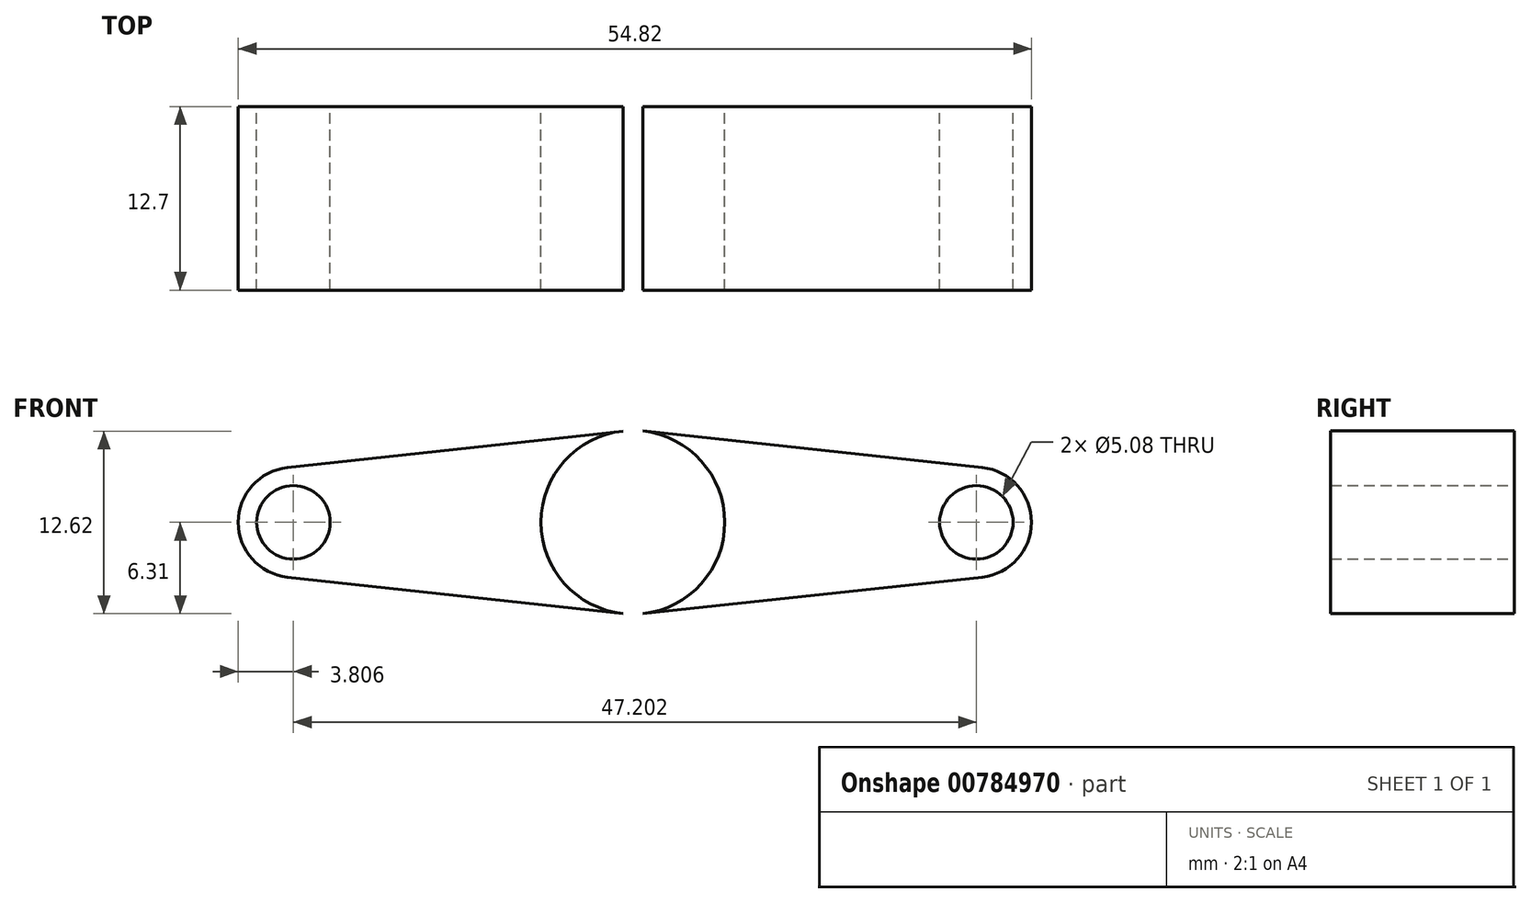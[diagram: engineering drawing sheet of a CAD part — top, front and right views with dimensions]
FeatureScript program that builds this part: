
annotation { "Feature Type Name" : "Feature", "Feature Type Description" : "" }
export const myFeature = defineFeature(function(context is Context, id is Id, definition is map)
    precondition{}
    {
        {
            var Q0;
            Q0=qCreatedBy(makeId("Front.planeOp"),FACE);
            var sketch = newSketch(context, id + "F0", { "sketchPlane" : qUnion([Q0])});
            skLineSegment(sketch, "E0", {"start": v(-23.46, 0) * mm, "end": v(23.74, 0) * mm});
            skCircle(sketch, "E1", {"center": v(23.74, 0) * mm, "radius": 3.81 * mm});
            skCircle(sketch, "E2", {"center": v(0, 0) * mm, "radius": 6.35 * mm});
            skCircle(sketch, "E3", {"center": v(-23.46, 0) * mm, "radius": 3.81 * mm});
            skLineSegment(sketch, "E4", {"start": v(-23.88, -3.79) * mm, "end": v(-0.69, -6.31) * mm});
            skLineSegment(sketch, "E5", {"start": v(-23.88, 3.79) * mm, "end": v(-0.69, 6.31) * mm});
            skLineSegment(sketch, "E6", {"start": v(0.68, 6.31) * mm, "end": v(24.15, 3.79) * mm});
            skLineSegment(sketch, "E7", {"start": v(0.68, -6.31) * mm, "end": v(24.15, -3.79) * mm});
            skCircle(sketch, "E8", {"center": v(-23.46, 0) * mm, "radius": 2.54 * mm});
            skCircle(sketch, "E9", {"center": v(0, 0) * mm, "radius": 5.08 * mm});
            skCircle(sketch, "E10", {"center": v(23.74, 0) * mm, "radius": 2.54 * mm});
            skSolve(sketch);
        }
        {
            var Q0;
            {var subQ5=sQuery(id+"F0.wireOp",EDGE,"E5");Q0=makeQuery(id+"F0.imprint","IMPRINT",FACE,{"disambiguationData":[TD([[makeQuery(id+"F0.imprint","IMPRINT",EDGE,{"derivedFrom":subQ5}),-1.0]])]});}
            var Q1;
            {var subQ5=sQuery(id+"F0.wireOp",EDGE,"E4");Q1=makeQuery(id+"F0.imprint","IMPRINT",FACE,{"disambiguationData":[TD([[makeQuery(id+"F0.imprint","IMPRINT",EDGE,{"derivedFrom":subQ5}),1.0]])]});}
            var Q2;
            {var subQ5=sQuery(id+"F0.wireOp",EDGE,"E6");Q2=makeQuery(id+"F0.imprint","IMPRINT",FACE,{"disambiguationData":[TD([[makeQuery(id+"F0.imprint","IMPRINT",EDGE,{"derivedFrom":subQ5}),-1.0]])]});}
            var Q3;
            {var subQ5=sQuery(id+"F0.wireOp",EDGE,"E7");Q3=makeQuery(id+"F0.imprint","IMPRINT",FACE,{"disambiguationData":[TD([[makeQuery(id+"F0.imprint","IMPRINT",EDGE,{"derivedFrom":subQ5}),1.0]])]});}
            var Q4;
            Q4=makeQuery(id+"F0.imprint","IMPRINT",FACE,{"disambiguationData":[TD([[makeQuery(id+"F0.imprint","IMPRINT",EDGE,{"derivedFrom":sQuery(id+"F0.wireOp",EDGE,"E10")}),-1.0]])]});
            var Q5;
            {var subQ0=sQuery(id+"F0.wireOp",EDGE,"E2");var subQ3=sQuery(id+"F0.wireOp",EDGE,"E0");var subQ7=makeQuery(id+"F0.imprint","INTERSECT",VERTEX,{"disambiguationData":[OD(0.0)],"derivedFrom":[subQ3,subQ0]});Q5=makeQuery(id+"F0.imprint","IMPRINT",FACE,{"disambiguationData":[TD([[makeQuery(id+"F0.imprint","IMPRINT",EDGE,{"disambiguationData":[TD([[subQ7,-1.0]])],"derivedFrom":subQ3}),1.0]])]});}
            var Q6;
            {var subQ0=sQuery(id+"F0.wireOp",EDGE,"E2");var subQ3=sQuery(id+"F0.wireOp",EDGE,"E0");var subQ4=makeQuery(id+"F0.imprint","INTERSECT",VERTEX,{"disambiguationData":[OD(0.0)],"derivedFrom":[subQ3,subQ0]});Q6=makeQuery(id+"F0.imprint","IMPRINT",FACE,{"disambiguationData":[TD([[makeQuery(id+"F0.imprint","IMPRINT",EDGE,{"disambiguationData":[TD([[subQ4,-1.0]])],"derivedFrom":subQ3}),-1.0]])]});}
            var Q7;
            Q7=makeQuery(id+"F0.imprint","IMPRINT",FACE,{"disambiguationData":[TD([[makeQuery(id+"F0.imprint","IMPRINT",EDGE,{"derivedFrom":sQuery(id+"F0.wireOp",EDGE,"E8")}),-1.0]])]});
            extrude(context, id + "F1", {"entities" : qUnion([Q0, Q1, Q2, Q3, Q4, Q5, Q6, Q7]), "depth" : 12.7 * mm, "offsetDistance" : 25.4 * mm});
        }
    });
